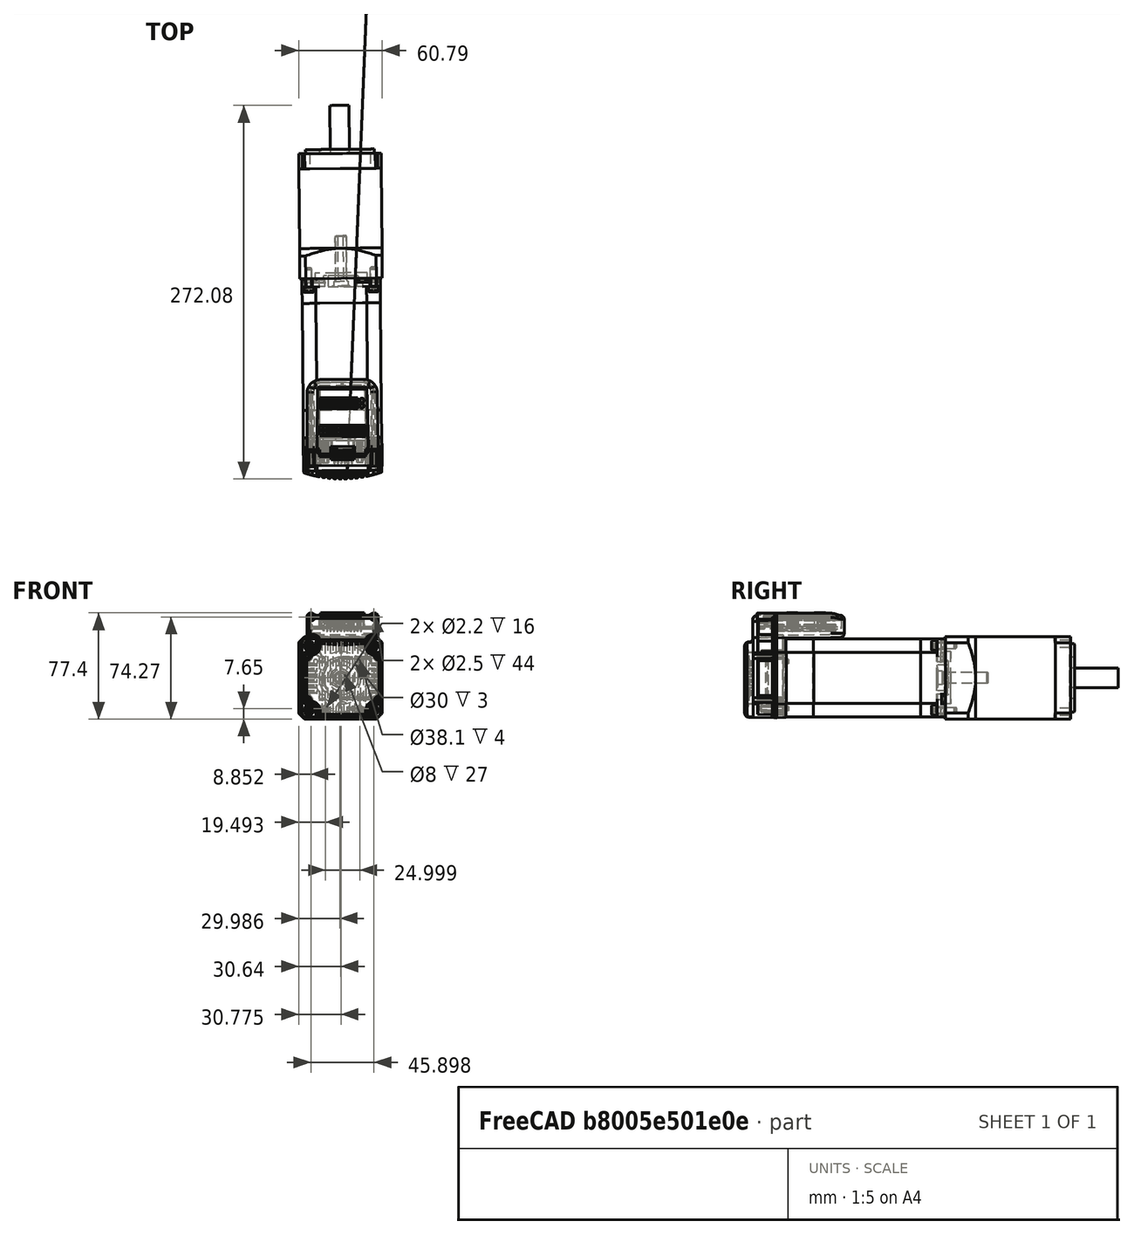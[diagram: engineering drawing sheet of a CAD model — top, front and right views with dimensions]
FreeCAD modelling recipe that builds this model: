
FCSTD DOCUMENT  (FreeCAD 0.19R23742 (Git))
Label: motor_gearbox_assembly
License: All rights reserved
LicenseURL: http://en.wikipedia.org/wiki/All_rights_reserved
objects: App::FeaturePython×14, Part::FeaturePython×6, App::DocumentObjectGroup×1
note: 6 computed .brp shape members not serialized (recipe doc carries the construction recipe); baked Part::Feature solids carry a one-line shape summary decoded from their .brp

FEATURE [Part::FeaturePython] b_100_001_Nema23_180W_Servo1_001_  label="100_001_Nema23_180W_Servo1_001"  # a2plus imported part (geometry in sourceFile) (typed FeaturePython)
  a2p_Version = V0.1
  fixedPosition = true
  objectType = a2pPart
  sourceFile = ./100_001_Nema23_180W_Servo.step
  subassemblyImport = false
  timeLastImport = 1.61628e+09
  updateColors = true
FEATURE [Part::FeaturePython] b_gearbox_001_  label="gearbox_001"  # a2plus imported part (geometry in sourceFile) (typed FeaturePython)
  Placement = pos=(-54.5054,195.523,-36.5) rot=(0.99999,0.004363,0;3.14159rad)
  a2p_Version = V0.1
  fixedPosition = false
  objectType = a2pPart
  sourceFile = ./gearbox.FCStd
  subassemblyImport = false
  timeLastImport = 1.61628e+09
  updateColors = true
FEATURE [App::FeaturePython] axisCoincident_001  label="axisCoincident_001__100_001_Nema23_180W_Servo1_001"  # a2plus constraint (typed FeaturePython)
  Object1 = b_gearbox_001_
  Object2 = b_100_001_Nema23_180W_Servo1_001_
  ParentTreeObject = -> b_gearbox_001_
  SubElement1 = Face48
  SubElement2 = Face1776
  Suppressed = false
  Type = axial
  directionConstraint = 0
  lockRotation = false
FEATURE [App::FeaturePython] axisCoincident_001_mirror  label="axisCoincident_001__gearbox_001"  # a2plus constraint (typed FeaturePython)
  Object1 = b_gearbox_001_
  Object2 = b_100_001_Nema23_180W_Servo1_001_
  ParentTreeObject = -> b_100_001_Nema23_180W_Servo1_001_
  SubElement1 = Face48
  SubElement2 = Face1776
  Suppressed = false
  Type = axial
  directionConstraint = 0
  lockRotation = false
FEATURE [App::FeaturePython] planesParallel_001  label="planesParallel_001__100_001_Nema23_180W_Servo1_001"  # a2plus constraint (typed FeaturePython)
  Object1 = b_gearbox_001_
  Object2 = b_100_001_Nema23_180W_Servo1_001_
  ParentTreeObject = -> b_gearbox_001_
  SubElement1 = Face27
  SubElement2 = Face1373
  Suppressed = false
  Type = planesParallel
  directionConstraint = 0
FEATURE [App::FeaturePython] planesParallel_001_mirror  label="planesParallel_001__gearbox_001"  # a2plus constraint (typed FeaturePython)
  Object1 = b_gearbox_001_
  Object2 = b_100_001_Nema23_180W_Servo1_001_
  ParentTreeObject = -> b_100_001_Nema23_180W_Servo1_001_
  SubElement1 = Face27
  SubElement2 = Face1373
  Suppressed = false
  Type = planesParallel
  directionConstraint = 0
FEATURE [App::FeaturePython] planeCoincident_001  label="planeCoincident_001__100_001_Nema23_180W_Servo1_001"  # a2plus constraint (typed FeaturePython)
  Object1 = b_gearbox_001_
  Object2 = b_100_001_Nema23_180W_Servo1_001_
  ParentTreeObject = -> b_gearbox_001_
  SubElement1 = Face34
  SubElement2 = Face1692
  Suppressed = false
  Type = plane
  directionConstraint = 0
  offset = 0
FEATURE [App::FeaturePython] planeCoincident_001_mirror  label="planeCoincident_001__gearbox_001"  # a2plus constraint (typed FeaturePython)
  Object1 = b_gearbox_001_
  Object2 = b_100_001_Nema23_180W_Servo1_001_
  ParentTreeObject = -> b_100_001_Nema23_180W_Servo1_001_
  SubElement1 = Face34
  SubElement2 = Face1692
  Suppressed = false
  Type = plane
  directionConstraint = 0
  offset = 0
FEATURE [Part::FeaturePython] Screw  label="M4x14-Screw"  # Fasteners workbench fastener (typed FeaturePython)
  Placement = pos=(-30.2559,109.732,-13) rot=(0.958745,0.205151,-0.196777;1.61109rad)
  diameter = 5
  invert = false
  length = 4
  lengthCustom = 14
  matchOuter = false
  offset = 0
  thread = false
  type = 32
FEATURE [App::FeaturePython] circularEdge_001  label="circularEdge_001__100_001_Nema23_180W_Servo1_001"  # a2plus constraint (typed FeaturePython)
  Object1 = Screw
  Object2 = b_100_001_Nema23_180W_Servo1_001_
  ParentTreeObject = -> Screw
  SubElement1 = Edge9
  SubElement2 = Edge4540
  Suppressed = false
  Type = circularEdge
  directionConstraint = 1
  lockRotation = true
  offset = 0
FEATURE [App::FeaturePython] circularEdge_001_mirror  label="circularEdge_001__M4x14-Screw"  # a2plus constraint (typed FeaturePython)
  Object1 = Screw
  Object2 = b_100_001_Nema23_180W_Servo1_001_
  ParentTreeObject = -> b_100_001_Nema23_180W_Servo1_001_
  SubElement1 = Edge9
  SubElement2 = Edge4540
  Suppressed = false
  Type = circularEdge
  directionConstraint = 1
  lockRotation = true
  offset = 0
FEATURE [Part::FeaturePython] Screw001  label="M4x14-Screw001"  # Fasteners workbench fastener (typed FeaturePython)
  Placement = pos=(-77.2541,109.322,-13) rot=(0.958745,0.205151,-0.196777;1.61109rad)
  diameter = 5
  invert = false
  length = 4
  lengthCustom = 14
  matchOuter = false
  offset = 0
  thread = false
  type = 32
FEATURE [Part::FeaturePython] Screw002  label="M4x14-Screw002"  # Fasteners workbench fastener (typed FeaturePython)
  Placement = pos=(-30.2559,109.732,-60) rot=(0.958745,0.205151,-0.196777;1.61109rad)
  diameter = 5
  invert = false
  length = 4
  lengthCustom = 14
  matchOuter = false
  offset = 0
  thread = false
  type = 32
FEATURE [Part::FeaturePython] Screw003  label="M4x14-Screw003"  # Fasteners workbench fastener (typed FeaturePython)
  Placement = pos=(-77.2541,109.322,-60) rot=(0.958745,0.205151,-0.196777;1.61109rad)
  diameter = 5
  invert = false
  length = 4
  lengthCustom = 14
  matchOuter = false
  offset = 0
  thread = false
  type = 32
FEATURE [App::DocumentObjectGroup] Group  label="Screws"
  Group = -> [Screw,circularEdge_001,Screw001,Screw002,Screw003]
FEATURE [App::FeaturePython] circularEdge_002  label="circularEdge_002__100_001_Nema23_180W_Servo1_001"  # a2plus constraint (typed FeaturePython)
  Object1 = Screw001
  Object2 = b_100_001_Nema23_180W_Servo1_001_
  ParentTreeObject = -> Screw001
  SubElement1 = Edge9
  SubElement2 = Edge4523
  Suppressed = false
  Type = circularEdge
  directionConstraint = 1
  lockRotation = true
  offset = 0
FEATURE [App::FeaturePython] circularEdge_002_mirror  label="circularEdge_002__M4x14-Screw001"  # a2plus constraint (typed FeaturePython)
  Object1 = Screw001
  Object2 = b_100_001_Nema23_180W_Servo1_001_
  ParentTreeObject = -> b_100_001_Nema23_180W_Servo1_001_
  SubElement1 = Edge9
  SubElement2 = Edge4523
  Suppressed = false
  Type = circularEdge
  directionConstraint = 1
  lockRotation = true
  offset = 0
FEATURE [App::FeaturePython] circularEdge_003  label="circularEdge_003__100_001_Nema23_180W_Servo1_001"  # a2plus constraint (typed FeaturePython)
  Object1 = Screw002
  Object2 = b_100_001_Nema23_180W_Servo1_001_
  ParentTreeObject = -> Screw002
  SubElement1 = Edge9
  SubElement2 = Edge4535
  Suppressed = false
  Type = circularEdge
  directionConstraint = 1
  lockRotation = true
  offset = 0
FEATURE [App::FeaturePython] circularEdge_003_mirror  label="circularEdge_003__M4x14-Screw002"  # a2plus constraint (typed FeaturePython)
  Object1 = Screw002
  Object2 = b_100_001_Nema23_180W_Servo1_001_
  ParentTreeObject = -> b_100_001_Nema23_180W_Servo1_001_
  SubElement1 = Edge9
  SubElement2 = Edge4535
  Suppressed = false
  Type = circularEdge
  directionConstraint = 1
  lockRotation = true
  offset = 0
FEATURE [App::FeaturePython] circularEdge_004  label="circularEdge_004__100_001_Nema23_180W_Servo1_001"  # a2plus constraint (typed FeaturePython)
  Object1 = Screw003
  Object2 = b_100_001_Nema23_180W_Servo1_001_
  ParentTreeObject = -> Screw003
  SubElement1 = Edge9
  SubElement2 = Edge4528
  Suppressed = false
  Type = circularEdge
  directionConstraint = 1
  lockRotation = true
  offset = 0
FEATURE [App::FeaturePython] circularEdge_004_mirror  label="circularEdge_004__M4x14-Screw003"  # a2plus constraint (typed FeaturePython)
  Object1 = Screw003
  Object2 = b_100_001_Nema23_180W_Servo1_001_
  ParentTreeObject = -> b_100_001_Nema23_180W_Servo1_001_
  SubElement1 = Edge9
  SubElement2 = Edge4528
  Suppressed = false
  Type = circularEdge
  directionConstraint = 1
  lockRotation = true
  offset = 0
